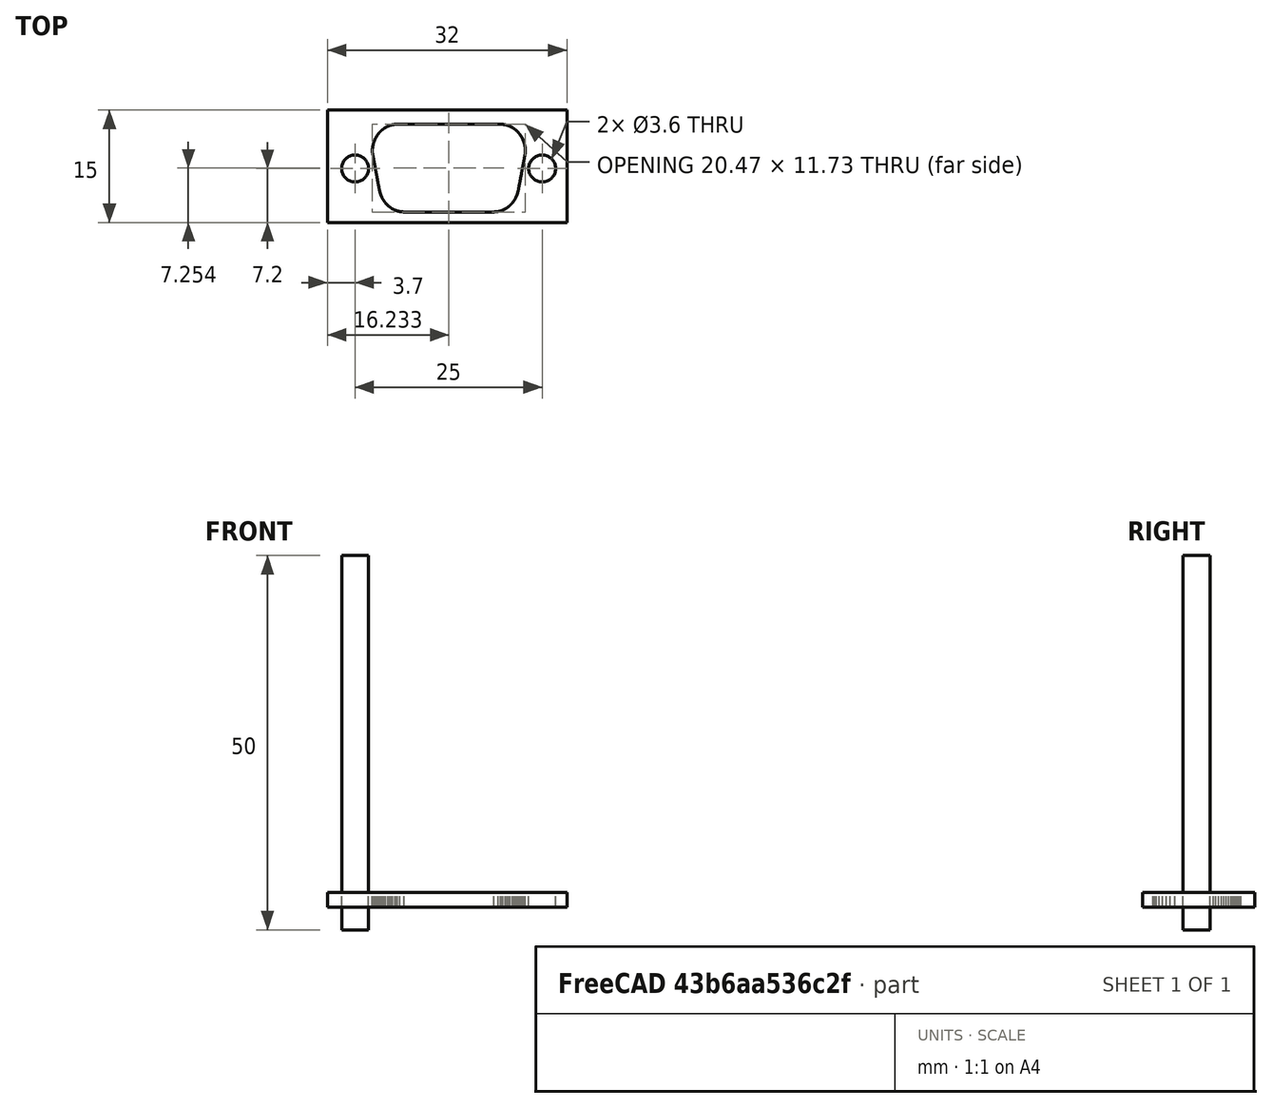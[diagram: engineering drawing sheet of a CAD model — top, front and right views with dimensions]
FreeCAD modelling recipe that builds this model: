
FCSTD DOCUMENT  (FreeCAD 0.19R23578 (Git))
Label: rs232_d9
License: All rights reserved
LicenseURL: http://en.wikipedia.org/wiki/All_rights_reserved
objects: Part::Cylinder×1, Part::FeaturePython×1, Part::Box×1, Part::Feature×1, Part::Compound×1, Part::Cut×1
note: 5 computed .brp shape members not serialized (recipe doc carries the construction recipe); baked Part::Feature solids carry a one-line shape summary decoded from their .brp

FEATURE [Part::Cylinder] Cylinder002  label="Cylinder"
  Angle = 360
  AttacherType = Attacher::AttachEngine3D
  Height = 50
  Placement = pos=(18.3,4.5,0) rot=(0,0,1;0rad)
  Radius = 1.8
FEATURE [Part::FeaturePython] Array002  # Draft array (typed FeaturePython)
  Angle = 360
  ArrayType = 0
  Axis = (0,0,1)
  Base = -> Cylinder002
  Center = (0,0,0)
  Count = 2
  ExpandArray = false
  Fuse = false
  IntervalAxis = (0,0,0)
  IntervalX = (25,0,0)
  IntervalY = (0,100,0)
  IntervalZ = (0,0,100)
  NumberCircles = 3
  NumberPolar = 5
  NumberX = 2
  NumberY = 1
  NumberZ = 1
  PlacementList = 2 placements: [(18.3,4.5,0),(43.3,4.5,0)]
  RadialDistance = 50
  ScaleList = (2) [(1,1,1),(1,1,1)]
  Symmetry = 1
  TangentialDistance = 25
FEATURE [Part::Box] Box033  label="test plate"
  AttacherType = Attacher::AttachEngine3D
  Height = 2
  Length = 32
  Placement = pos=(14.6,-2.7,3) rot=(0,0,1;0rad)
  Width = 15
FEATURE [Part::Feature] Clone001  label="Cut002001.005"
  Placement = pos=(0,-0.5,0) rot=(0,0,1;0rad)
  shape: bbox 20.47 x 11.73 x 40 mm, 60 faces (baked)
FEATURE [Part::Compound] Compound  label="db9 hole compound"
  Links = -> [Array002,Clone001]
FEATURE [Part::Cut] Cut002002  label="test plate cut"
  Base = -> Box033
  Tool = -> Compound
